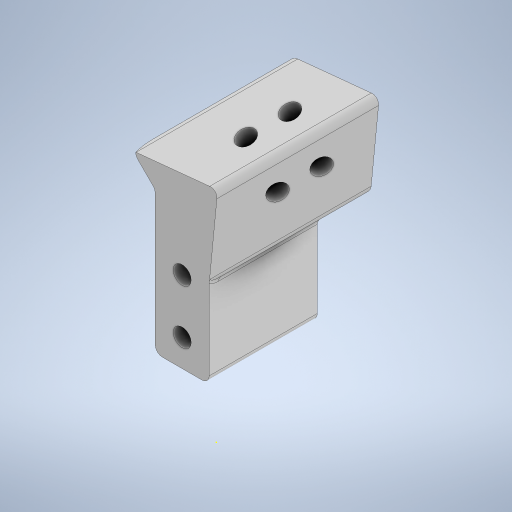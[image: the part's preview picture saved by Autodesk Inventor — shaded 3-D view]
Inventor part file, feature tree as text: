
AUTODESK INVENTOR PART (.ipt)
format: ipt  version: 2024.3 (Build 283343000, 343)  size: 434,688 bytes
history: native  units: mm
features: sketch x15, extrude x11, projected_geometry x7, hole x3, other x1, fillet x1
ambient origin geometry x8: Origin, YZ Plane, XZ Plane, XY Plane, X Axis, Y Axis, Z Axis, Center Point
bodies: Body1 (feature_tree)
feature tree (38):
  other  "ソリッド1"
  extrude  "押し出し1"  Depth=60.0mm
  hole  "穴1"  [1 undecoded]
  extrude  "押し出し2"  Depth=30.0mm TaperAngle=0.0deg
  extrude  "押し出し11"  Depth=7.5mm
  extrude  "押し出し12"  Depth=7.5mm
  extrude  "押し出し17"  Depth=10.5mm
  extrude  "押し出し18"  Depth=10.5mm
  sketch  "スケッチ27"
  extrude  "押し出し19"  Depth=15.0mm
  hole  "穴4"  [1 undecoded]
  hole  "穴5"  [1 undecoded]
  extrude  "押し出し22"  Depth=26.0mm
  extrude  "押し出し23"  Depth=7.5mm
  fillet  "フィレット2"  Radius=7.5mm
  extrude  "押し出し24"  Depth=7.5mm
  extrude  "押し出し25"  Depth=30.0mm
  sketch  "スケッチ1"
  sketch  "スケッチ2"
  sketch  "スケッチ3"
  projected_geometry  "投影ループ1"
  sketch  "スケッチ15"
  projected_geometry  "投影ループ10"
  sketch  "スケッチ16"
  projected_geometry  "投影ループ11"
  sketch  "スケッチ25"
  projected_geometry  "投影ループ18"
  sketch  "スケッチ26"
  projected_geometry  "投影ループ19"
  sketch  "スケッチ28"
  sketch  "スケッチ29"
  sketch  "スケッチ30"
  sketch  "スケッチ33"
  sketch  "スケッチ34"
  projected_geometry  "投影ループ22"
  sketch  "スケッチ35"
  projected_geometry  "投影ループ23"
  sketch  "スケッチ36"
note: 3 required parameter values undecoded (feature->parameter linkage not recoverable at this tier; creation-order binding heuristic only, values carry confidence <= 0.55)
